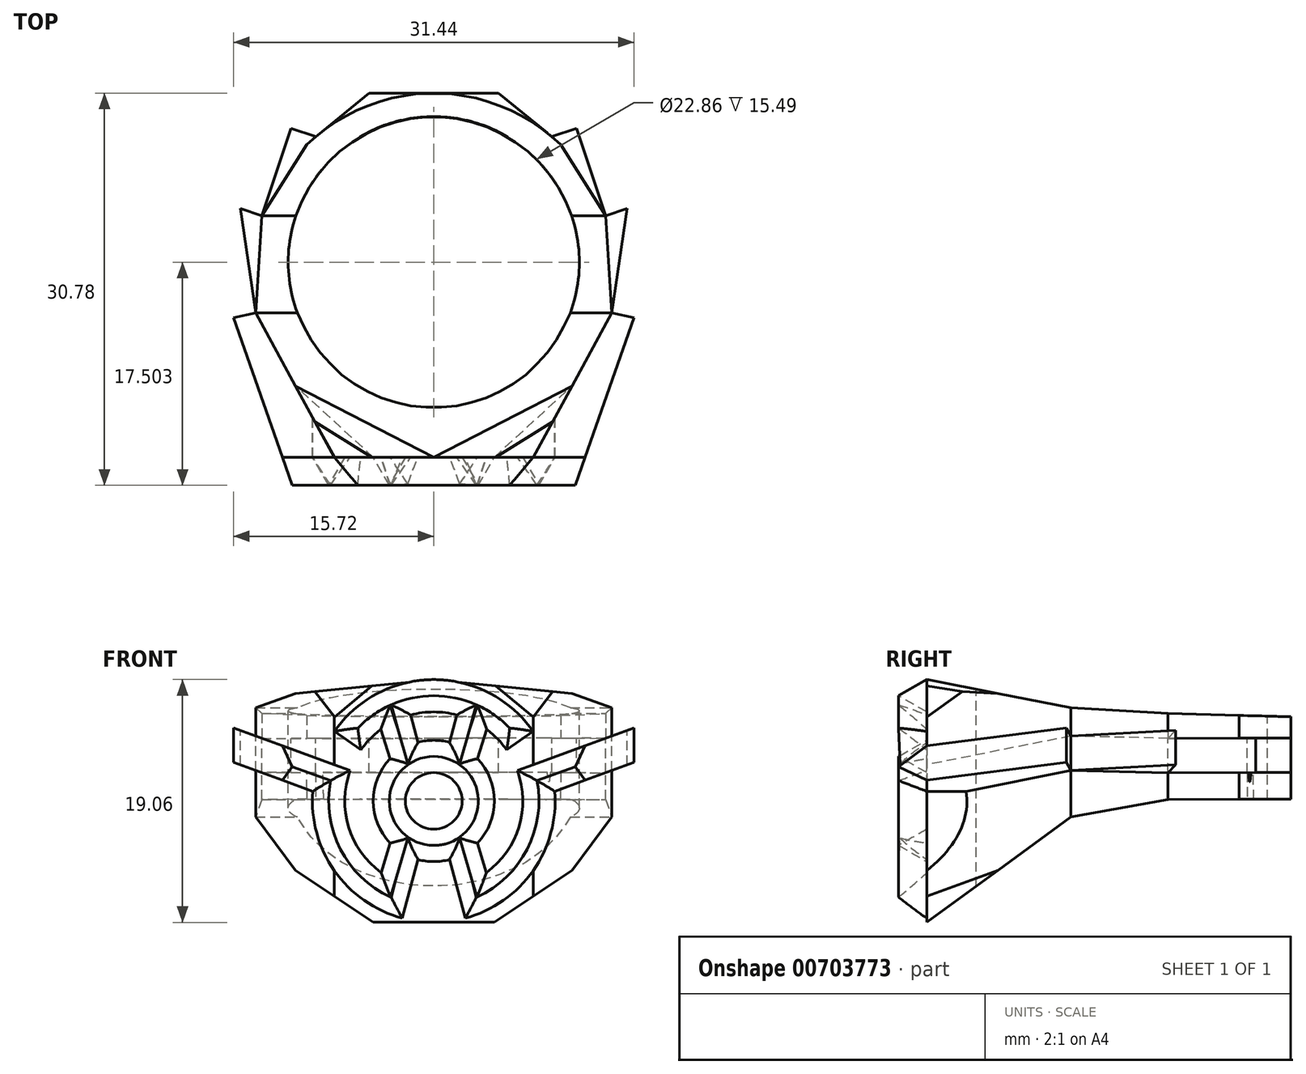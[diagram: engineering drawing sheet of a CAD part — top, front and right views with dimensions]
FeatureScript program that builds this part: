
annotation { "Feature Type Name" : "Feature", "Feature Type Description" : "" }
export const myFeature = defineFeature(function(context is Context, id is Id, definition is map)
    precondition{}
    {
        {
            var Q0;
            Q0=qCreatedBy(makeId("Front.planeOp"),FACE);
            var sketch = newSketch(context, id + "F0", { "sketchPlane" : qUnion([Q0])});
            skCircle(sketch, "E0", {"center": v(0, 0) * mm, "radius": 4.76 * mm, "construction": true});
            skArc(sketch, "E1", {"start": v(7.8, 5.46) * mm, "mid": v(0, 9.53) * mm, "end": v(-7.8, 5.46) * mm, "construction": true});
            skArc(sketch, "E2", {"start": v(-8.95, 3.26) * mm, "mid": v(-8.45, -4.4) * mm, "end": v(-2.47, -9.2) * mm, "construction": true});
            skArc(sketch, "E3", {"start": v(2.47, -9.2) * mm, "mid": v(8.45, -4.4) * mm, "end": v(8.95, 3.26) * mm, "construction": true});
            skLineSegment(sketch, "E4", {"start": v(-2.47, 9.2) * mm, "end": v(2.47, -9.2) * mm, "construction": true});
            skLineSegment(sketch, "E5", {"start": v(-2.47, -9.2) * mm, "end": v(2.47, 9.2) * mm, "construction": true});
            skLineSegment(sketch, "E6", {"start": v(0, 0) * mm, "end": v(-7.8, 5.46) * mm, "construction": true});
            skLineSegment(sketch, "E7", {"start": v(0, 0) * mm, "end": v(7.8, 5.46) * mm, "construction": true});
            skLineSegment(sketch, "E8", {"start": v(-8.95, 3.26) * mm, "end": v(0, 0) * mm, "construction": true});
            skLineSegment(sketch, "E9", {"start": v(0, 0) * mm, "end": v(8.95, 3.26) * mm, "construction": true});
            skCircle(sketch, "E10", {"center": v(0, 0) * mm, "radius": 2.22 * mm, "construction": true});
            skCircle(sketch, "E11", {"center": v(0, 0) * mm, "radius": 6.99 * mm, "construction": true});
            skSolve(sketch);
        }
        {
            var Q0;
            Q0=qCreatedBy(makeId("Front.planeOp"),FACE);
            var sketch = newSketch(context, id + "F1", { "sketchPlane" : qUnion([Q0])});
            skArc(sketch, "E12", {"start": v(7.8, 5.46) * mm, "mid": v(0, 9.53) * mm, "end": v(-7.8, 5.46) * mm});
            skArc(sketch, "E13", {"start": v(-9.5, 0.75) * mm, "mid": v(-7.78, -5.5) * mm, "end": v(-2.47, -9.2) * mm});
            skArc(sketch, "E14", {"start": v(2.47, -9.2) * mm, "mid": v(7.78, -5.5) * mm, "end": v(9.5, 0.75) * mm});
            skLineSegment(sketch, "E15", {"start": v(-2.47, -9.2) * mm, "end": v(-1.23, -4.6) * mm});
            skLineSegment(sketch, "E16", {"start": v(2.47, -9.2) * mm, "end": v(1.23, -4.6) * mm});
            skArc(sketch, "E17", {"start": v(-1.23, -4.6) * mm, "mid": v(0, -4.76) * mm, "end": v(1.23, -4.6) * mm});
            skLineSegment(sketch, "E18", {"start": v(-7.8, 5.46) * mm, "end": v(-5.72, 4) * mm});
            skLineSegment(sketch, "E19", {"start": v(7.8, 5.46) * mm, "end": v(5.72, 4) * mm});
            skCircle(sketch, "E20", {"center": v(0, 0) * mm, "radius": 2.22 * mm});
            skLineSegment(sketch, "E21", {"start": v(-1.23, 4.6) * mm, "end": v(-1.8, 6.75) * mm});
            skLineSegment(sketch, "E22", {"start": v(1.23, 4.6) * mm, "end": v(1.8, 6.75) * mm});
            skLineSegment(sketch, "E23", {"start": v(-6.56, 2.39) * mm, "end": v(-20.88, 7.6) * mm});
            skLineSegment(sketch, "E24", {"start": v(6.56, 2.39) * mm, "end": v(20.88, 7.6) * mm});
            skLineSegment(sketch, "E25", {"start": v(-20.88, 7.6) * mm, "end": v(-21.75, 5.21) * mm});
            skLineSegment(sketch, "E26", {"start": v(-9.5, 0.75) * mm, "end": v(-21.75, 5.21) * mm});
            skLineSegment(sketch, "E27", {"start": v(20.88, 7.6) * mm, "end": v(21.75, 5.21) * mm});
            skLineSegment(sketch, "E28", {"start": v(21.75, 5.21) * mm, "end": v(9.5, 0.75) * mm});
            skArc(sketch, "E29", {"start": v(-6.56, 2.39) * mm, "mid": v(-6.68, -2.03) * mm, "end": v(-4.13, -5.63) * mm});
            skArc(sketch, "E30", {"start": v(4.13, -5.63) * mm, "mid": v(6.68, -2.03) * mm, "end": v(6.56, 2.39) * mm});
            skLineSegment(sketch, "E31", {"start": v(-4.13, -5.63) * mm, "end": v(-3.42, -3.31) * mm});
            skLineSegment(sketch, "E32", {"start": v(4.13, -5.63) * mm, "end": v(3.42, -3.31) * mm});
            skArc(sketch, "E33", {"start": v(1.23, 4.6) * mm, "mid": v(0, 4.76) * mm, "end": v(-1.23, 4.6) * mm});
            skArc(sketch, "E34", {"start": v(1.8, 6.75) * mm, "mid": v(0, 6.99) * mm, "end": v(-1.8, 6.75) * mm});
            skArc(sketch, "E35", {"start": v(-4.15, 5.62) * mm, "mid": v(-5, 4.88) * mm, "end": v(-5.72, 4) * mm});
            skArc(sketch, "E36", {"start": v(5.72, 4) * mm, "mid": v(5, 4.88) * mm, "end": v(4.15, 5.62) * mm});
            skLineSegment(sketch, "E37", {"start": v(-4.15, 5.62) * mm, "end": v(-3.42, 3.31) * mm});
            skLineSegment(sketch, "E38", {"start": v(4.15, 5.62) * mm, "end": v(3.42, 3.31) * mm});
            skArc(sketch, "E39", {"start": v(-3.42, 3.31) * mm, "mid": v(-4.76, 0) * mm, "end": v(-3.42, -3.31) * mm});
            skArc(sketch, "E40", {"start": v(3.42, -3.31) * mm, "mid": v(4.76, 0) * mm, "end": v(3.42, 3.31) * mm});
            skSolve(sketch);
        }
        {
            var Q0;
            Q0=qSketchRegion(id+"F1",true);
            extrude(context, id + "F2", {"entities" : qUnion([Q0]), "depth" : 3.17 * mm, "offsetDistance" : 25.4 * mm, "hasDraft" : true, "draftAngle" : 30 * degree, "draftPullDirection" : true, "hasSecondDirection" : true, "secondDirectionOppositeDirection" : true, "secondDirectionDepth" : 38.1 * mm});
        }
        {
            var Q0;
            Q0=makeQuery(id+"F2.opExtrude","CAP_FACE",FACE,{"disambiguationData":[OSD([sQuery(id+"F1.wireOp",EDGE,"E12"),sQuery(id+"F1.wireOp",EDGE,"E13"),sQuery(id+"F1.wireOp",EDGE,"E14"),sQuery(id+"F1.wireOp",EDGE,"E15"),sQuery(id+"F1.wireOp",EDGE,"E16"),sQuery(id+"F1.wireOp",EDGE,"E17"),sQuery(id+"F1.wireOp",EDGE,"E18"),sQuery(id+"F1.wireOp",EDGE,"E19"),sQuery(id+"F1.wireOp",EDGE,"E20"),sQuery(id+"F1.wireOp",EDGE,"E21"),sQuery(id+"F1.wireOp",EDGE,"E22"),sQuery(id+"F1.wireOp",EDGE,"E23"),sQuery(id+"F1.wireOp",EDGE,"E24"),sQuery(id+"F1.wireOp",EDGE,"E25"),sQuery(id+"F1.wireOp",EDGE,"E26"),sQuery(id+"F1.wireOp",EDGE,"E27"),sQuery(id+"F1.wireOp",EDGE,"E28"),sQuery(id+"F1.wireOp",EDGE,"E29"),sQuery(id+"F1.wireOp",EDGE,"E30"),sQuery(id+"F1.wireOp",EDGE,"E31"),sQuery(id+"F1.wireOp",EDGE,"E32"),sQuery(id+"F1.wireOp",EDGE,"E33"),sQuery(id+"F1.wireOp",EDGE,"E34"),sQuery(id+"F1.wireOp",EDGE,"E35"),sQuery(id+"F1.wireOp",EDGE,"E36"),sQuery(id+"F1.wireOp",EDGE,"E37"),sQuery(id+"F1.wireOp",EDGE,"E38"),sQuery(id+"F1.wireOp",EDGE,"E39"),sQuery(id+"F1.wireOp",EDGE,"E40")])],"isStart":true});
            var sketch = newSketch(context, id + "F3", { "sketchPlane" : qUnion([Q0])});
            skLineSegment(sketch, "E41", {"start": v(-20.88, 7.6) * mm, "end": v(0, 0) * mm});
            skLineSegment(sketch, "E42", {"start": v(20.88, 7.6) * mm, "end": v(0, 0) * mm});
            skLineSegment(sketch, "E43", {"start": v(-20.88, 7.6) * mm, "end": v(-21.75, 5.21) * mm});
            skLineSegment(sketch, "E44", {"start": v(20.88, 7.6) * mm, "end": v(21.75, 5.21) * mm});
            skLineSegment(sketch, "E45", {"start": v(21.75, 5.21) * mm, "end": v(0, -2.7) * mm});
            skLineSegment(sketch, "E46", {"start": v(-21.75, 5.21) * mm, "end": v(0, -2.7) * mm});
            skSolve(sketch);
        }
        {
            var Q0;
            Q0=qSketchRegion(id+"F3",true);
            extrude(context, id + "F4", {"entities" : qUnion([Q0]), "operationType" : NewBodyOperationType.ADD, "oppositeDirection" : true, "depth" : 19.05 * mm, "offsetDistance" : 25.4 * mm});
        }
        {
            var Q0;
            Q0=makeQuery(id+"F4.boolean.opBoolean","MERGE",FACE,{"derivedFrom":[makeQuery(id+"F2.opExtrude","CAP_FACE",FACE,{"disambiguationData":[OSD([sQuery(id+"F1.wireOp",EDGE,"E12"),sQuery(id+"F1.wireOp",EDGE,"E13"),sQuery(id+"F1.wireOp",EDGE,"E14"),sQuery(id+"F1.wireOp",EDGE,"E15"),sQuery(id+"F1.wireOp",EDGE,"E16"),sQuery(id+"F1.wireOp",EDGE,"E17"),sQuery(id+"F1.wireOp",EDGE,"E18"),sQuery(id+"F1.wireOp",EDGE,"E19"),sQuery(id+"F1.wireOp",EDGE,"E20"),sQuery(id+"F1.wireOp",EDGE,"E21"),sQuery(id+"F1.wireOp",EDGE,"E22"),sQuery(id+"F1.wireOp",EDGE,"E23"),sQuery(id+"F1.wireOp",EDGE,"E24"),sQuery(id+"F1.wireOp",EDGE,"E25"),sQuery(id+"F1.wireOp",EDGE,"E26"),sQuery(id+"F1.wireOp",EDGE,"E27"),sQuery(id+"F1.wireOp",EDGE,"E28"),sQuery(id+"F1.wireOp",EDGE,"E29"),sQuery(id+"F1.wireOp",EDGE,"E30"),sQuery(id+"F1.wireOp",EDGE,"E31"),sQuery(id+"F1.wireOp",EDGE,"E32"),sQuery(id+"F1.wireOp",EDGE,"E33"),sQuery(id+"F1.wireOp",EDGE,"E34"),sQuery(id+"F1.wireOp",EDGE,"E35"),sQuery(id+"F1.wireOp",EDGE,"E36"),sQuery(id+"F1.wireOp",EDGE,"E37"),sQuery(id+"F1.wireOp",EDGE,"E38"),sQuery(id+"F1.wireOp",EDGE,"E39"),sQuery(id+"F1.wireOp",EDGE,"E40")])],"isStart":true}),makeQuery(id+"F4.opExtrude","CAP_FACE",FACE,{"disambiguationData":[OSD([sQuery(id+"F3.wireOp",EDGE,"E41"),sQuery(id+"F3.wireOp",EDGE,"E42"),sQuery(id+"F3.wireOp",EDGE,"E43"),sQuery(id+"F3.wireOp",EDGE,"E44"),sQuery(id+"F3.wireOp",EDGE,"E45"),sQuery(id+"F3.wireOp",EDGE,"E46")])],"isStart":true})]});
            var sketch = newSketch(context, id + "F5", { "sketchPlane" : qUnion([Q0])});
            skArc(sketch, "E47", {"start": v(8.95, 3.26) * mm, "mid": v(0, 9.53) * mm, "end": v(-8.95, 3.26) * mm});
            skArc(sketch, "E48", {"start": v(-9.5, 0.75) * mm, "mid": v(0, -9.52) * mm, "end": v(9.5, 0.75) * mm});
            skLineSegment(sketch, "E49", {"start": v(-8.95, 3.26) * mm, "end": v(0, 0) * mm});
            skLineSegment(sketch, "E50", {"start": v(0, 0) * mm, "end": v(8.95, 3.26) * mm});
            skLineSegment(sketch, "E51", {"start": v(-9.5, 0.75) * mm, "end": v(0, -2.7) * mm});
            skLineSegment(sketch, "E52", {"start": v(0, -2.7) * mm, "end": v(9.5, 0.75) * mm});
            skSolve(sketch);
        }
        {
            var Q0;
            Q0=qSketchRegion(id+"F5",true);
            extrude(context, id + "F6", {"entities" : qUnion([Q0]), "operationType" : NewBodyOperationType.REMOVE, "oppositeDirection" : true, "depth" : 19.05 * mm, "offsetDistance" : 25.4 * mm});
        }
        {
            var Q0;
            Q0=qCreatedBy(makeId("Top.planeOp"),FACE);
            var sketch = newSketch(context, id + "F7", { "sketchPlane" : qUnion([Q0])});
            skLineSegment(sketch, "E53", {"start": v(-11.11, -2.2) * mm, "end": v(11.11, -2.2) * mm});
            skPoint(sketch, "E54", {"position": v(0, -2.2) * mm});
            skLineSegment(sketch, "E55", {"start": v(-11.11, -2.2) * mm, "end": v(-13.98, 11.33) * mm, "construction": true});
            skLineSegment(sketch, "E56", {"start": v(11.11, -2.2) * mm, "end": v(13.98, 11.33) * mm, "construction": true});
            skCircle(sketch, "E57", {"center": v(0, 14.29) * mm, "radius": 14.29 * mm, "construction": true});
            skLineSegment(sketch, "E58", {"start": v(11.11, -2.2) * mm, "end": v(15.72, 10.96) * mm});
            skLineSegment(sketch, "E59", {"start": v(15.72, 10.96) * mm, "end": v(13.98, 11.33) * mm});
            skLineSegment(sketch, "E60", {"start": v(-11.11, -2.2) * mm, "end": v(-15.72, 10.96) * mm});
            skLineSegment(sketch, "E61", {"start": v(-15.72, 10.96) * mm, "end": v(-13.98, 11.33) * mm});
            skPoint(sketch, "E62", {"position": v(-13.5, 18.95) * mm});
            skPoint(sketch, "E63", {"position": v(13.5, 18.95) * mm});
            skLineSegment(sketch, "E64", {"start": v(-13.5, 18.95) * mm, "end": v(-15.19, 19.53) * mm});
            skLineSegment(sketch, "E65", {"start": v(13.5, 18.95) * mm, "end": v(15.19, 19.53) * mm});
            skLineSegment(sketch, "E66", {"start": v(-13.98, 11.33) * mm, "end": v(-15.19, 19.53) * mm});
            skLineSegment(sketch, "E67", {"start": v(13.98, 11.33) * mm, "end": v(15.19, 19.53) * mm});
            skPoint(sketch, "E68", {"position": v(-9.96, 24.54) * mm});
            skPoint(sketch, "E69", {"position": v(9.96, 24.54) * mm});
            skLineSegment(sketch, "E70", {"start": v(-9.96, 24.54) * mm, "end": v(-11.2, 25.81) * mm});
            skLineSegment(sketch, "E71", {"start": v(9.96, 24.54) * mm, "end": v(11.2, 25.81) * mm});
            skLineSegment(sketch, "E72", {"start": v(-13.5, 18.95) * mm, "end": v(-11.2, 25.81) * mm});
            skLineSegment(sketch, "E73", {"start": v(11.2, 25.81) * mm, "end": v(13.5, 18.95) * mm});
            skCircle(sketch, "E74", {"center": v(0, 14.29) * mm, "radius": 38.1 * mm});
            skArc(sketch, "E75", {"start": v(9.96, 24.54) * mm, "mid": v(0, 28.58) * mm, "end": v(-9.96, 24.54) * mm});
            skSolve(sketch);
        }
        {
            var Q0;
            Q0=qSketchRegion(id+"F7",true);
            extrude(context, id + "F8", {"entities" : qUnion([Q0]), "operationType" : NewBodyOperationType.REMOVE, "oppositeDirection" : true, "depth" : 25.4 * mm, "offsetDistance" : 25.4 * mm, "hasSecondDirection" : true, "secondDirectionOppositeDirection" : false, "secondDirectionDepth" : 25.4 * mm});
        }
        {
            var Q0;
            Q0=qCreatedBy(makeId("Top.planeOp"),FACE);
            var sketch = newSketch(context, id + "F9", { "sketchPlane" : qUnion([Q0])});
            skCircle(sketch, "E76", {"center": v(0, 14.29) * mm, "radius": 14.29 * mm, "construction": true});
            skLineSegment(sketch, "E77", {"start": v(-13.98, 11.33) * mm, "end": v(-7.8, 0) * mm});
            skLineSegment(sketch, "E78", {"start": v(7.8, 0) * mm, "end": v(13.98, 11.33) * mm});
            skLineSegment(sketch, "E79", {"start": v(-7.8, 0) * mm, "end": v(7.8, 0) * mm});
            skLineSegment(sketch, "E80", {"start": v(-13.98, 11.33) * mm, "end": v(-13.5, 18.95) * mm});
            skLineSegment(sketch, "E81", {"start": v(13.98, 11.33) * mm, "end": v(13.5, 18.95) * mm});
            skLineSegment(sketch, "E82", {"start": v(-13.5, 18.95) * mm, "end": v(-9.96, 24.54) * mm});
            skLineSegment(sketch, "E83", {"start": v(13.5, 18.95) * mm, "end": v(9.96, 24.54) * mm});
            skArc(sketch, "E84", {"start": v(9.96, 24.54) * mm, "mid": v(0, 28.58) * mm, "end": v(-9.96, 24.54) * mm});
            skSolve(sketch);
        }
        {
            var Q0;
            Q0=qSketchRegion(id+"F9",true);
            extrude(context, id + "F10", {"entities" : qUnion([Q0]), "operationType" : NewBodyOperationType.ADD, "depth" : 9.52 * mm, "offsetDistance" : 25.4 * mm, "hasSecondDirection" : true, "secondDirectionOppositeDirection" : true, "secondDirectionDepth" : 9.52 * mm});
        }
        {
            var Q0;
            Q0=makeQuery(id+"F10.opExtrude","CAP_FACE",FACE,{"disambiguationData":[OSD([sQuery(id+"F9.wireOp",EDGE,"E77"),sQuery(id+"F9.wireOp",EDGE,"E78"),sQuery(id+"F9.wireOp",EDGE,"E79"),sQuery(id+"F9.wireOp",EDGE,"E80"),sQuery(id+"F9.wireOp",EDGE,"E81"),sQuery(id+"F9.wireOp",EDGE,"E82"),sQuery(id+"F9.wireOp",EDGE,"E83"),sQuery(id+"F9.wireOp",EDGE,"E84")])],"isStart":false});
            var sketch = newSketch(context, id + "F11", { "sketchPlane" : qUnion([Q0])});
            skCircle(sketch, "E85", {"center": v(0, 15.3) * mm, "radius": 11.43 * mm});
            skSolve(sketch);
        }
        {
            var Q0;
            Q0=qSketchRegion(id+"F11",true);
            extrude(context, id + "F12", {"entities" : qUnion([Q0]), "operationType" : NewBodyOperationType.REMOVE, "endBound" : BoundingType.THROUGH_ALL, "oppositeDirection" : true, "depth" : 25.4 * mm, "offsetDistance" : 25.4 * mm});
        }
        {
            var Q0;
            Q0=qCreatedBy(makeId("Right.planeOp"),FACE);
            cPlane(context, id + "F13", {"entities" : qUnion([Q0]), "cplaneType" : CPlaneType.OFFSET, "offset" : 17.78 * mm, "width" : 152.4 * mm, "height" : 152.4 * mm});
        }
        {
            var Q0;
            Q0=qCreatedBy(id+"F13.planeOp",FACE);
            var sketch = newSketch(context, id + "F14", { "sketchPlane" : qUnion([Q0])});
            skLineSegment(sketch, "E86", {"start": v(0, 9.53) * mm, "end": v(11.33, 7.3) * mm});
            skLineSegment(sketch, "E87", {"start": v(0, 9.53) * mm, "end": v(30.66, 9.53) * mm});
            skLineSegment(sketch, "E88", {"start": v(0, -9.53) * mm, "end": v(11.33, -1.27) * mm});
            skLineSegment(sketch, "E89", {"start": v(0, -9.53) * mm, "end": v(31.52, -9.53) * mm});
            skLineSegment(sketch, "E90", {"start": v(30.64, 0.14) * mm, "end": v(31.52, -9.53) * mm});
            skLineSegment(sketch, "E91", {"start": v(30.52, 6.56) * mm, "end": v(30.66, 9.53) * mm});
            skLineSegment(sketch, "E92", {"start": v(11.33, -1.27) * mm, "end": v(18.95, 0.12) * mm});
            skLineSegment(sketch, "E93", {"start": v(11.33, 7.3) * mm, "end": v(18.94, 6.86) * mm});
            skLineSegment(sketch, "E94", {"start": v(18.95, 0.12) * mm, "end": v(30.64, 0.14) * mm});
            skLineSegment(sketch, "E95", {"start": v(18.94, 6.86) * mm, "end": v(30.52, 6.56) * mm});
            skSolve(sketch);
        }
        {
            var Q0;
            Q0 = qSketchRegion(id + "F14", true);
            extrude(context, id + "F15", {"entities" : qUnion([Q0]), "operationType" : NewBodyOperationType.REMOVE, "endBound" : BoundingType.THROUGH_ALL, "oppositeDirection" : true, "depth" : 25.4 * mm, "offsetDistance" : 25.4 * mm});
        }
        {
            var Q0;
            {var subQ0=sQuery(id+"F9.wireOp",EDGE,"E77");var subQ1=sQuery(id+"F9.wireOp",EDGE,"E79");var subQ2=sQuery(id+"F9.wireOp",EDGE,"E78");Q0=makeQuery(id+"F10.boolean.opBoolean","SPLIT",FACE,{"disambiguationData":[TD([makeQuery(id+"F2.opExtrude","SWEPT_FACE",FACE,{"disambiguationData":[OSD([sQuery(id+"F1.wireOp",EDGE,"E13")])]}),makeQuery(id+"F2.opExtrude","SWEPT_FACE",FACE,{"disambiguationData":[OSD([sQuery(id+"F1.wireOp",EDGE,"E14")])]}),makeQuery(id+"F2.opExtrude","SWEPT_FACE",FACE,{"disambiguationData":[OSD([sQuery(id+"F1.wireOp",EDGE,"E15")])]}),makeQuery(id+"F2.opExtrude","SWEPT_FACE",FACE,{"disambiguationData":[OSD([sQuery(id+"F1.wireOp",EDGE,"E16")])]}),makeQuery(id+"F2.opExtrude","SWEPT_FACE",FACE,{"disambiguationData":[OSD([sQuery(id+"F1.wireOp",EDGE,"E17")])]}),makeQuery(id+"F2.opExtrude","SWEPT_FACE",FACE,{"disambiguationData":[OSD([sQuery(id+"F1.wireOp",EDGE,"E33")])]}),makeQuery(id+"F2.opExtrude","SWEPT_FACE",FACE,{"disambiguationData":[OSD([sQuery(id+"F1.wireOp",EDGE,"E39")])]}),makeQuery(id+"F2.opExtrude","SWEPT_FACE",FACE,{"disambiguationData":[OSD([sQuery(id+"F1.wireOp",EDGE,"E40")])]}),makeQuery(id+"F10.opExtrude","SWEPT_FACE",FACE,{"disambiguationData":[OSD([subQ0])]}),makeQuery(id+"F10.opExtrude","CAP_FACE",FACE,{"disambiguationData":[OSD([subQ0,subQ2,subQ1,sQuery(id+"F9.wireOp",EDGE,"E80"),sQuery(id+"F9.wireOp",EDGE,"E81"),sQuery(id+"F9.wireOp",EDGE,"E82"),sQuery(id+"F9.wireOp",EDGE,"E83"),sQuery(id+"F9.wireOp",EDGE,"E84")])],"isStart":true}),makeQuery(id+"F10.opExtrude","SWEPT_FACE",FACE,{"disambiguationData":[OSD([subQ2])]})])],"derivedFrom":makeQuery(id+"F10.opExtrude","SWEPT_FACE",FACE,{"disambiguationData":[OSD([subQ1])]})});}
            var sketch = newSketch(context, id + "F16", { "sketchPlane" : qUnion([Q0])});
            skLineSegment(sketch, "E96", {"start": v(-4.75, -9.53) * mm, "end": v(-10.85, -9.53) * mm});
            skPoint(sketch, "E97", {"position": v(-7.8, -9.53) * mm});
            skLineSegment(sketch, "E98", {"start": v(-10.85, -9.53) * mm, "end": v(-10.85, -5.45) * mm});
            skLineSegment(sketch, "E99", {"start": v(-10.85, -5.45) * mm, "end": v(-4.75, -9.53) * mm});
            skLineSegment(sketch, "E100", {"start": v(4.75, -9.53) * mm, "end": v(10.85, -9.53) * mm});
            skPoint(sketch, "E101", {"position": v(7.8, -9.53) * mm});
            skLineSegment(sketch, "E102", {"start": v(10.85, -9.53) * mm, "end": v(10.85, -5.45) * mm});
            skLineSegment(sketch, "E103", {"start": v(10.85, -5.45) * mm, "end": v(4.75, -9.53) * mm});
            skLineSegment(sketch, "E104", {"start": v(-10.85, 8.43) * mm, "end": v(0, 9.53) * mm});
            skLineSegment(sketch, "E105", {"start": v(0, 9.53) * mm, "end": v(10.85, 8.43) * mm});
            skLineSegment(sketch, "E106", {"start": v(-10.85, 8.43) * mm, "end": v(-10.85, 11.02) * mm});
            skLineSegment(sketch, "E107", {"start": v(-10.85, 11.02) * mm, "end": v(10.85, 11.02) * mm});
            skLineSegment(sketch, "E108", {"start": v(10.85, 11.02) * mm, "end": v(10.85, 8.43) * mm});
            skSolve(sketch);
        }
        {
            var Q0;
            Q0 = qSketchRegion(id + "F16", true);
            extrude(context, id + "F17", {"entities" : qUnion([Q0]), "operationType" : NewBodyOperationType.REMOVE, "endBound" : BoundingType.THROUGH_ALL, "oppositeDirection" : true, "depth" : 25.4 * mm, "offsetDistance" : 25.4 * mm});
        }
        {
            var Q0;
            Q0=makeQuery(id+"F8.boolean.opBoolean","COPY",FACE,{"derivedFrom":makeQuery(id+"F8.opExtrude","SWEPT_FACE",FACE,{"disambiguationData":[OSD([sQuery(id+"F7.wireOp",EDGE,"E73")])]})});
            var sketch = newSketch(context, id + "F18", { "sketchPlane" : qUnion([Q0])});
            skLineSegment(sketch, "E109", {"start": v(13.65, 4.92) * mm, "end": v(20.89, 4.93) * mm});
            skLineSegment(sketch, "E110", {"start": v(13.65, 2.21) * mm, "end": v(20.89, 2.23) * mm});
            skLineSegment(sketch, "E111", {"start": v(13.65, 2.21) * mm, "end": v(13.65, 4.92) * mm});
            skLineSegment(sketch, "E112", {"start": v(20.89, 2.23) * mm, "end": v(20.89, 4.93) * mm});
            skSolve(sketch);
        }
        {
            var Q0;
            Q0 = qSketchRegion(id + "F18", true);
            extrude(context, id + "F19", {"entities" : qUnion([Q0]), "operationType" : NewBodyOperationType.ADD, "oppositeDirection" : true, "depth" : 2.3 * mm, "offsetDistance" : 25.4 * mm});
        }
        {
            var Q0;
            Q0=makeQuery(id+"F8.boolean.opBoolean","COPY",FACE,{"derivedFrom":makeQuery(id+"F8.opExtrude","SWEPT_FACE",FACE,{"disambiguationData":[OSD([sQuery(id+"F7.wireOp",EDGE,"E72")])]})});
            var sketch = newSketch(context, id + "F20", { "sketchPlane" : qUnion([Q0])});
            skLineSegment(sketch, "E113", {"start": v(-13.65, 2.21) * mm, "end": v(-13.65, 4.92) * mm});
            skLineSegment(sketch, "E114", {"start": v(-13.65, 4.92) * mm, "end": v(-20.89, 4.9) * mm});
            skLineSegment(sketch, "E115", {"start": v(-13.65, 2.21) * mm, "end": v(-20.89, 2.23) * mm});
            skLineSegment(sketch, "E116", {"start": v(-20.89, 2.23) * mm, "end": v(-20.89, 4.9) * mm});
            skSolve(sketch);
        }
        {
            var Q0;
            Q0 = qSketchRegion(id + "F20", true);
            extrude(context, id + "F21", {"entities" : qUnion([Q0]), "operationType" : NewBodyOperationType.ADD, "oppositeDirection" : true, "depth" : 2.3 * mm, "offsetDistance" : 25.4 * mm});
        }
        {
            var Q0;
            Q0=makeQuery(id+"F19.opExtrude","SWEPT_FACE",FACE,{"disambiguationData":[OSD([sQuery(id+"F18.wireOp",EDGE,"E110")])]});
            var sketch = newSketch(context, id + "F22", { "sketchPlane" : qUnion([Q0])});
            skLineSegment(sketch, "E117", {"start": v(9.27, -25.17) * mm, "end": v(11.2, -25.81) * mm});
            skLineSegment(sketch, "E118", {"start": v(11.2, -25.81) * mm, "end": v(13.5, -18.95) * mm});
            skLineSegment(sketch, "E119", {"start": v(9.27, -25.17) * mm, "end": v(9.95, -24.54) * mm});
            skLineSegment(sketch, "E120", {"start": v(9.95, -24.54) * mm, "end": v(13.5, -18.95) * mm});
            skLineSegment(sketch, "E121", {"start": v(-11.2, -25.81) * mm, "end": v(-13.5, -18.95) * mm});
            skLineSegment(sketch, "E122", {"start": v(-13.5, -18.95) * mm, "end": v(-9.96, -24.54) * mm});
            skLineSegment(sketch, "E123", {"start": v(-11.2, -25.81) * mm, "end": v(-9.27, -25.17) * mm});
            skLineSegment(sketch, "E124", {"start": v(-9.27, -25.17) * mm, "end": v(-9.96, -24.54) * mm});
            skSolve(sketch);
        }
        {
            var Q0;
            Q0 = qSketchRegion(id + "F22", true);
            extrude(context, id + "F23", {"entities" : qUnion([Q0]), "operationType" : NewBodyOperationType.REMOVE, "depth" : 25.4 * mm, "offsetDistance" : 25.4 * mm});
        }
        {
            var Q0;
            Q0=qCreatedBy(makeId("Front.planeOp"),FACE);
            cPlane(context, id + "F24", {"entities" : qUnion([Q0]), "cplaneType" : CPlaneType.OFFSET, "offset" : 25.15 * mm, "oppositeDirection" : true, "width" : 152.4 * mm, "height" : 152.4 * mm});
        }
        {
            var Q0;
            Q0=qCreatedBy(id+"F24.planeOp",FACE);
            var sketch = newSketch(context, id + "F25", { "sketchPlane" : qUnion([Q0])});
            skLineSegment(sketch, "E125", {"start": v(9.27, 4.93) * mm, "end": v(-9.27, 4.9) * mm});
            skLineSegment(sketch, "E126", {"start": v(9.27, 4.93) * mm, "end": v(9.27, 2.23) * mm});
            skLineSegment(sketch, "E127", {"start": v(9.27, 2.23) * mm, "end": v(-9.27, 2.23) * mm});
            skLineSegment(sketch, "E128", {"start": v(-9.27, 2.23) * mm, "end": v(-9.27, 4.9) * mm});
            skSolve(sketch);
        }
        {
            var Q0;
            Q0 = qSketchRegion(id + "F25", true);
            extrude(context, id + "F26", {"entities" : qUnion([Q0]), "operationType" : NewBodyOperationType.ADD, "oppositeDirection" : true, "depth" : 3.8 * mm, "offsetDistance" : 25.4 * mm});
        }
        {
            var Q0;
            {var subQ2=sQuery(id+"F25.wireOp",EDGE,"E125");Q0=makeQuery(id+"F26.boolean.opBoolean","SPLIT",FACE,{"disambiguationData":[TD([makeQuery(id+"F8.boolean.opBoolean","COPY",FACE,{"derivedFrom":makeQuery(id+"F8.opExtrude","SWEPT_FACE",FACE,{"disambiguationData":[OSD([sQuery(id+"F7.wireOp",EDGE,"E75")])]})})])],"derivedFrom":makeQuery(id+"F26.opExtrude","SWEPT_FACE",FACE,{"disambiguationData":[OSD([subQ2])]})});}
            var sketch = newSketch(context, id + "F27", { "sketchPlane" : qUnion([Q0])});
            skLineSegment(sketch, "E129", {"start": v(5.82, 25.15) * mm, "end": v(-5.8, 25.15) * mm});
            skArc(sketch, "E130", {"start": v(5.82, 25.15) * mm, "mid": v(0, 26.73) * mm, "end": v(-5.8, 25.15) * mm});
            skLineSegment(sketch, "E131", {"start": v(-5.07, 28.58) * mm, "end": v(5.1, 28.58) * mm});
            skPoint(sketch, "E132", {"position": v(0.01, 28.58) * mm});
            skLineSegment(sketch, "E133", {"start": v(-9.26, 25.16) * mm, "end": v(-5.07, 28.58) * mm});
            skLineSegment(sketch, "E134", {"start": v(9.28, 25.16) * mm, "end": v(5.1, 28.58) * mm});
            skLineSegment(sketch, "E135", {"start": v(-9.26, 25.16) * mm, "end": v(-9.26, 28.96) * mm});
            skLineSegment(sketch, "E136", {"start": v(9.28, 25.16) * mm, "end": v(9.28, 28.96) * mm});
            skLineSegment(sketch, "E137", {"start": v(9.28, 28.96) * mm, "end": v(-9.26, 28.96) * mm});
            skSolve(sketch);
        }
        {
            var Q0;
            Q0 = qSketchRegion(id + "F27", true);
            extrude(context, id + "F28", {"entities" : qUnion([Q0]), "operationType" : NewBodyOperationType.REMOVE, "oppositeDirection" : true, "depth" : 25.4 * mm, "offsetDistance" : 25.4 * mm});
        }
        {
            var Q0;
            Q0=makeQuery(id+"F17.boolean.opBoolean","COPY",FACE,{"derivedFrom":makeQuery(id+"F17.opExtrude","SWEPT_FACE",FACE,{"disambiguationData":[OSD([sQuery(id+"F16.wireOp",EDGE,"E104")])]})});
            var sketch = newSketch(context, id + "F29", { "sketchPlane" : qUnion([Q0])});
            skLineSegment(sketch, "E138", {"start": v(-3.92, 0) * mm, "end": v(-8.42, 2.8) * mm});
            skLineSegment(sketch, "E139", {"start": v(-8.42, 2.8) * mm, "end": v(-9.26, -4.15) * mm});
            skLineSegment(sketch, "E140", {"start": v(-3.92, 0) * mm, "end": v(-9.26, -4.15) * mm});
            skLineSegment(sketch, "E141", {"start": v(-9.26, -4.15) * mm, "end": v(-6.17, 1.4) * mm, "construction": true});
            skSolve(sketch);
        }
        {
            var Q0;
            Q0 = qSketchRegion(id + "F29", true);
            extrude(context, id + "F30", {"entities" : qUnion([Q0]), "operationType" : NewBodyOperationType.REMOVE, "oppositeDirection" : true, "depth" : 25.4 * mm, "offsetDistance" : 25.4 * mm, "hasDraft" : true, "draftAngle" : 38 * degree, "draftPullDirection" : true});
        }
        {
            var Q0;
            Q0=makeQuery(id+"F17.boolean.opBoolean","COPY",FACE,{"derivedFrom":makeQuery(id+"F17.opExtrude","SWEPT_FACE",FACE,{"disambiguationData":[OSD([sQuery(id+"F16.wireOp",EDGE,"E105")])]})});
            var sketch = newSketch(context, id + "F31", { "sketchPlane" : qUnion([Q0])});
            skLineSegment(sketch, "E142", {"start": v(8.42, 2.8) * mm, "end": v(3.92, 0) * mm});
            skLineSegment(sketch, "E143", {"start": v(8.42, 2.8) * mm, "end": v(9.78, -3.83) * mm});
            skLineSegment(sketch, "E144", {"start": v(9.78, -3.83) * mm, "end": v(3.92, 0) * mm});
            skLineSegment(sketch, "E145", {"start": v(9.78, -3.83) * mm, "end": v(6.17, 1.4) * mm, "construction": true});
            skSolve(sketch);
        }
        {
            var Q0;
            Q0 = qSketchRegion(id + "F31", true);
            extrude(context, id + "F32", {"entities" : qUnion([Q0]), "operationType" : NewBodyOperationType.REMOVE, "oppositeDirection" : true, "depth" : 25.4 * mm, "offsetDistance" : 25.4 * mm, "hasDraft" : true, "draftAngle" : 38 * degree, "draftPullDirection" : true});
        }
    });
